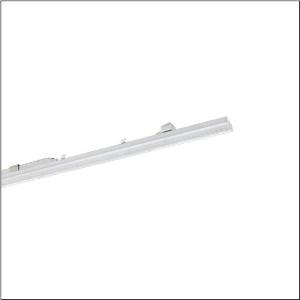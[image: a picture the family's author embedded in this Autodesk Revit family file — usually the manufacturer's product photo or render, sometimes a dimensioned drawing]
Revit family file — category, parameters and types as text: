
# Revit family: tl_l_5wd7a8p0h2c5
name_source: partatom
category: Lighting Fixtures
units: mm (PartAtom-declared; Revit-internal decimal feet)

## family parameters
Cut with Voids When Loaded = No
Host = Face
Light Source = No
Part Type = Normal
Room Calculation Point = No
Round Connector Dimension = Use Diameter
Shared = No

## types (1)
- --- (1 x LED, 9800 lm, 63.4 W, 4000K)
    Apparent Load = 63 VA
    CIE Flux Codes = 49 84 98 100 100
    Color Rendering = 80
    Color Temperature = 4000K
    Default Elevation = 1800 mm
    Description = TL L, luminaire insert, of sheet steel, galvanised, coil coated, white, length: 1.500mm, width: 66mm, height: 67mm, surge protection,LED light colour: 840, control gear: DALI, with terminal, 5-pole, mains connection: 230..240V, AC, 50/60Hz, rated input power: 30W, micro fuse,primary optical cover: cover, of PMMA, light emission: direct distribution, protection rating (complete): as luminaire, insulation class (complete): insulation class I (protective earthing), certification: CE, impact resistance: IK06, permissible ambient temperature for indoor applications: -35..+35°C, standard: NMF01, packaging unit: 1 piece
    Height = 120 mm
    Lamp = 1 x LED
    Lamp Light Flux = 9800 lm
    Lamp Power = 63.4 W
    Lamp count = 1
    Length = 1690 mm
    Luminous efficacy = 155 lm/W
    Manufacturer = Siteco
    ModVariant = No
    Model = 5WD7A8P0H2C5
    Mounting Place = Ceiling
    Mounting Type = Pendant
    Number of Poles = 1
    OnlyDefault = Yes
    Power Factor = 1
    Product Name = TL L
    Product group = luminaire insert
    ProductGroupID = 901
    Protection Class = Protection class I
    Protection Degree = Degree of protection
    RLX_Detail_Level = 1
    RLX_Emergency_Light_Flux = 0 lm
    RLX_Emergency_Type = 0
    RLX_Emergency_Type_DB = No
    RlxData = <blob elided: 17281 chars, md5=638d080c>
    Socket = socket
    Standby Power = 0 W
    System Light Flux = 9800 lm
    System Power = 63 W
    Type Comments = factory setting: luminous flux: 100 % | dim-lin: 254 | 420 mA
    Type Image = l_1294382.jpg
    URL = http://relux.com
    VarID = @adj_016735
    Voltage = 0 V
    Weight = 0.00 kg
    Width = 208 mm

## geometry (parser evidence)
native form markers: Blend x4, Sweep x10
no freeform markers — native parametric forms only
